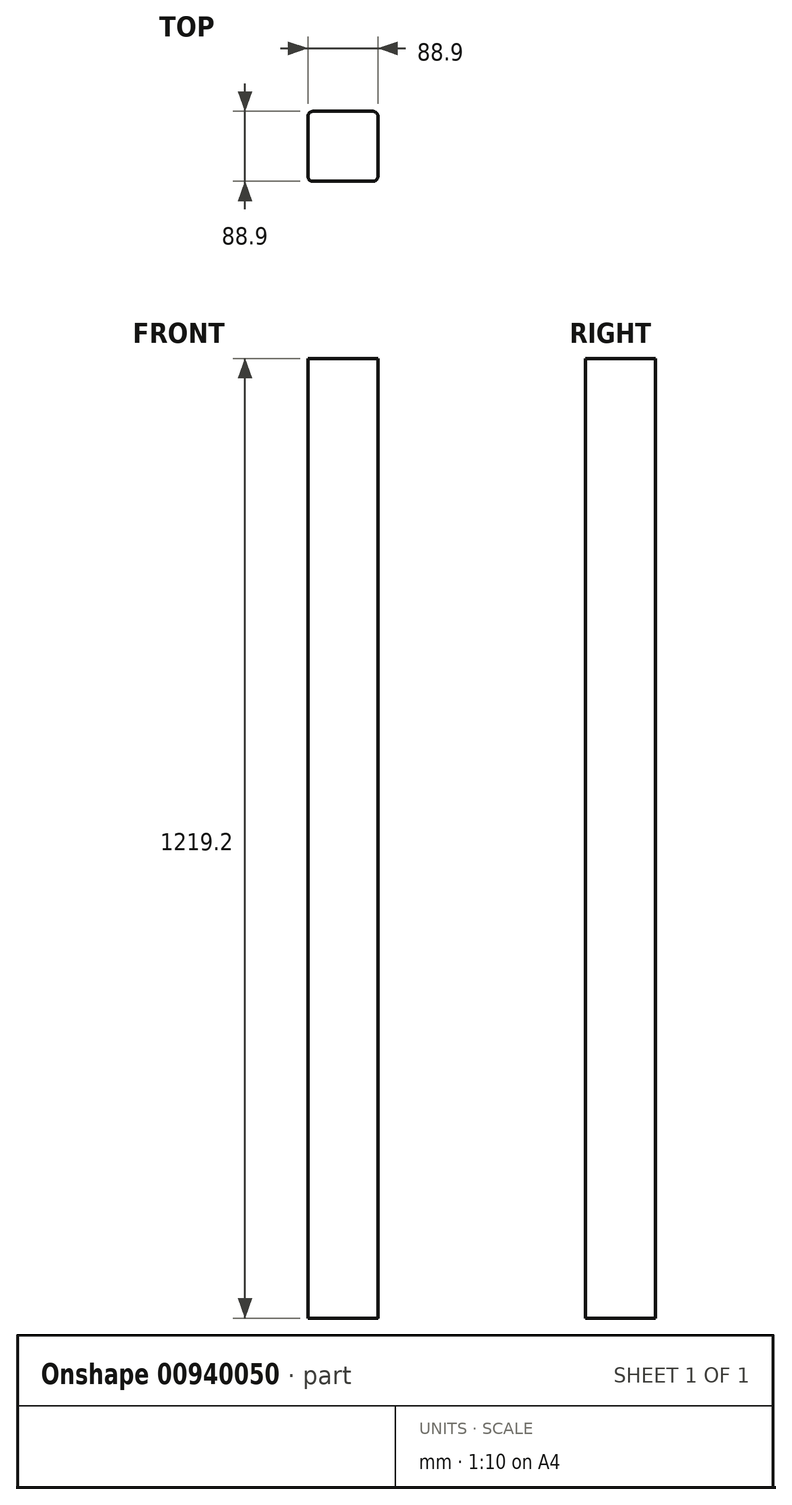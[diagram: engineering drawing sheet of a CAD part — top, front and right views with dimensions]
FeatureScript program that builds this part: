
annotation { "Feature Type Name" : "Feature", "Feature Type Description" : "" }
export const myFeature = defineFeature(function(context is Context, id is Id, definition is map)
    precondition{}
    {
        {
            var Q0;
            Q0=qCreatedBy(makeId("Top.planeOp"),FACE);
            var sketch = newSketch(context, id + "F0", { "sketchPlane" : qUnion([Q0])});
            skLineSegment(sketch, "E0.bottom", {"start": v(38.1, 44.45) * mm, "end": v(-38.1, 44.45) * mm});
            skLineSegment(sketch, "E0.top", {"start": v(38.1, -44.45) * mm, "end": v(-38.1, -44.45) * mm});
            skLineSegment(sketch, "E0.left", {"start": v(44.45, 38.1) * mm, "end": v(44.45, -38.1) * mm});
            skLineSegment(sketch, "E0.right", {"start": v(-44.45, 38.1) * mm, "end": v(-44.45, -38.1) * mm});
            skPoint(sketch, "E0.middle", {"position": v(0, 0) * mm});
            skPoint(sketch, "E1.visualSharp", {"position": v(-44.45, 44.45) * mm});
            skArc(sketch, "E1.filletArc", {"start": v(-38.1, 44.45) * mm, "mid": v(-42.6, 42.6) * mm, "end": v(-44.45, 38.1) * mm});
            skPoint(sketch, "E2.visualSharp", {"position": v(-44.45, -44.45) * mm});
            skArc(sketch, "E2.filletArc", {"start": v(-44.45, -38.1) * mm, "mid": v(-42.6, -42.6) * mm, "end": v(-38.1, -44.45) * mm});
            skPoint(sketch, "E3.visualSharp", {"position": v(44.45, -44.45) * mm});
            skArc(sketch, "E3.filletArc", {"start": v(38.1, -44.45) * mm, "mid": v(42.6, -42.6) * mm, "end": v(44.45, -38.1) * mm});
            skPoint(sketch, "E4.visualSharp", {"position": v(44.45, 44.45) * mm});
            skArc(sketch, "E4.filletArc", {"start": v(44.45, 38.1) * mm, "mid": v(42.6, 42.6) * mm, "end": v(38.1, 44.45) * mm});
            skSolve(sketch);
        }
        {
            var Q0;
            Q0 = qSketchRegion(id + "F0", true);
            extrude(context, id + "F1", {"entities" : qUnion([Q0]), "depth" : 1219.2 * mm, "offsetDistance" : 25.4 * mm});
        }
    });
